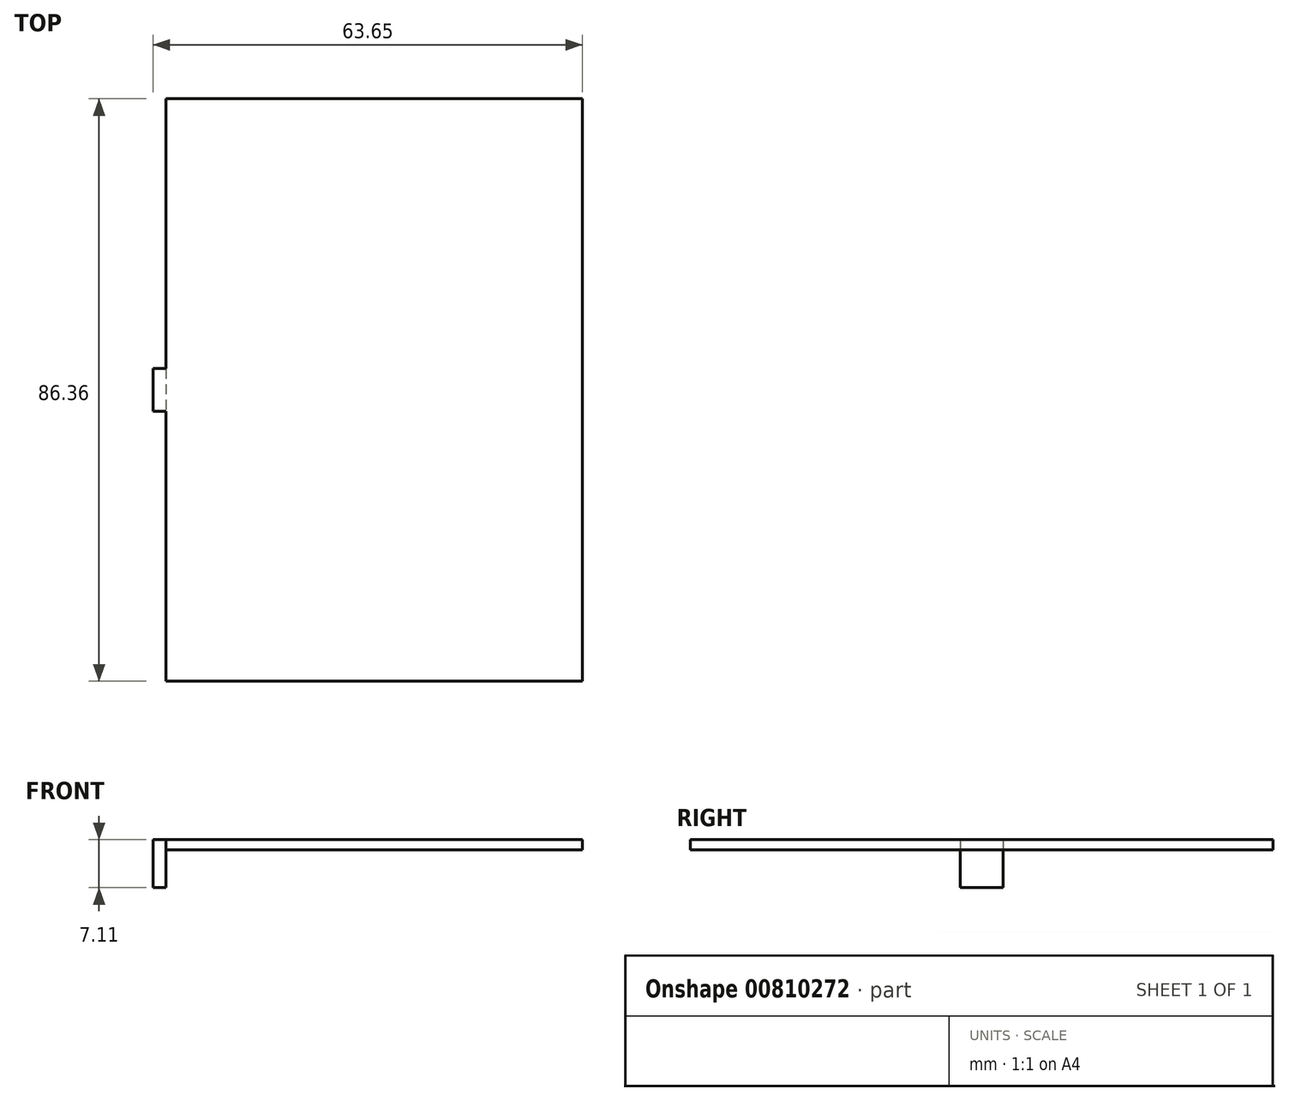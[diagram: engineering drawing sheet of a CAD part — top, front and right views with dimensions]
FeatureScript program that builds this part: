
annotation { "Feature Type Name" : "Feature", "Feature Type Description" : "" }
export const myFeature = defineFeature(function(context is Context, id is Id, definition is map)
    precondition{}
    {
        {
            var Q0;
            Q0=qCreatedBy(makeId("Top.planeOp"),FACE);
            var sketch = newSketch(context, id + "F0", { "sketchPlane" : qUnion([Q0])});
            skLineSegment(sketch, "E0.bottom", {"start": v(-30.86, 43.18) * mm, "end": v(30.86, 43.18) * mm});
            skLineSegment(sketch, "E0.top", {"start": v(-30.86, -43.18) * mm, "end": v(30.86, -43.18) * mm});
            skLineSegment(sketch, "E0.left", {"start": v(-30.86, 43.18) * mm, "end": v(-30.86, -43.18) * mm});
            skLineSegment(sketch, "E0.right", {"start": v(30.86, 43.18) * mm, "end": v(30.86, -43.18) * mm});
            skPoint(sketch, "E0.middle", {"position": v(0, 0) * mm});
            skSolve(sketch);
        }
        {
            var Q0;
            Q0 = qSketchRegion(id + "F0", true);
            extrude(context, id + "F1", {"entities" : qUnion([Q0]), "depth" : 1.52 * mm, "offsetDistance" : 25.4 * mm});
        }
        {
            var Q0;
            Q0=makeQuery(id+"F1.opExtrude","SWEPT_FACE",FACE,{"disambiguationData":[OSD([sQuery(id+"F0.wireOp",EDGE,"E0.left")])]});
            var sketch = newSketch(context, id + "F2", { "sketchPlane" : qUnion([Q0])});
            skPoint(sketch, "E1.middle", {"position": v(0, 0) * mm});
            skLineSegment(sketch, "E2.bottom", {"start": v(-3.17, 1.52) * mm, "end": v(3.18, 1.52) * mm});
            skLineSegment(sketch, "E2.top", {"start": v(-3.17, -1.52) * mm, "end": v(3.18, -1.52) * mm});
            skLineSegment(sketch, "E2.left", {"start": v(-3.17, 1.52) * mm, "end": v(-3.17, -1.52) * mm});
            skLineSegment(sketch, "E2.right", {"start": v(3.18, 1.52) * mm, "end": v(3.18, -1.52) * mm});
            skSolve(sketch);
        }
        {
            var Q0;
            Q0 = qSketchRegion(id + "F2", true);
            extrude(context, id + "F3", {"entities" : qUnion([Q0]), "operationType" : NewBodyOperationType.ADD, "depth" : 1.93 * mm, "offsetDistance" : 25.4 * mm});
        }
        {
            var Q0;
            Q0=makeQuery(id+"F3.opExtrude","SWEPT_FACE",FACE,{"disambiguationData":[OSD([sQuery(id+"F2.wireOp",EDGE,"E2.top")])]});
            var sketch = newSketch(context, id + "F4", { "sketchPlane" : qUnion([Q0])});
            skLineSegment(sketch, "E3.bottom", {"start": v(-32.8, 3.18) * mm, "end": v(-30.86, 3.18) * mm});
            skLineSegment(sketch, "E3.top", {"start": v(-32.8, -3.18) * mm, "end": v(-30.86, -3.18) * mm});
            skLineSegment(sketch, "E3.left", {"start": v(-32.8, 3.18) * mm, "end": v(-32.8, -3.18) * mm});
            skLineSegment(sketch, "E3.right", {"start": v(-30.86, 3.18) * mm, "end": v(-30.86, -3.18) * mm});
            skPoint(sketch, "E3.middle", {"position": v(-31.83, 0) * mm});
            skPoint(sketch, "E3.middle.positionSnap0", {"position": v(-31.83, -3.17) * mm});
            skPoint(sketch, "E3.centerSnap0", {"position": v(-31.83, -3.17) * mm});
            skSolve(sketch);
        }
        {
            var Q0;
            Q0=makeQuery(id+"F4.imprint","IMPRINT",FACE,{"disambiguationData":[TD([[makeQuery(id+"F4.imprint","IMPRINT",EDGE,{"derivedFrom":sQuery(id+"F4.wireOp",EDGE,"E3.bottom")}),-1.0]])]});
            extrude(context, id + "F5", {"entities" : qUnion([Q0]), "operationType" : NewBodyOperationType.ADD, "depth" : 4.06 * mm, "offsetDistance" : 25.4 * mm});
        }
    });
